# Revit family: Keilhauer-Epix-Counter_Stool_Sled_Base-1
name_source: partatom
category: Furniture
revit_build: Autodesk Revit 2016 (Build: 20151007_0715(x64)
units: mm (PartAtom-declared; Revit-internal decimal feet)

## family parameters
Always vertical = Yes
Cut with Voids When Loaded = No
OmniClass Number = 23.40.70.14.64.11
OmniClass Title = Office Furniture
Room Calculation Point = No
Shared = No
Work Plane-Based = No

## types (2) — shared parameters
Assembly Code = E2020200
Depth = 21 27/32"
Height = 37 49/64"
Manufacturer = Keilhauer
Product Documentation Link = https://keilhauer.com
Seat Pad = Yes
Type Comments = Epix
URL = https://keilhauer.com
Width = 19 11/16"

## per-type parameters (varying)
| type | Arms | Description |
| 76265 | No | Counter stool, formed felt shell with seatpad, sled base |
| 76275 | Yes | Counter stool, formed felt shell with arms and seatpad, sled base |

note: column(s) folded — value = type name in every type: Model

## geometry (parser evidence)
native form markers: Sweep x4
no freeform markers — native parametric forms only
